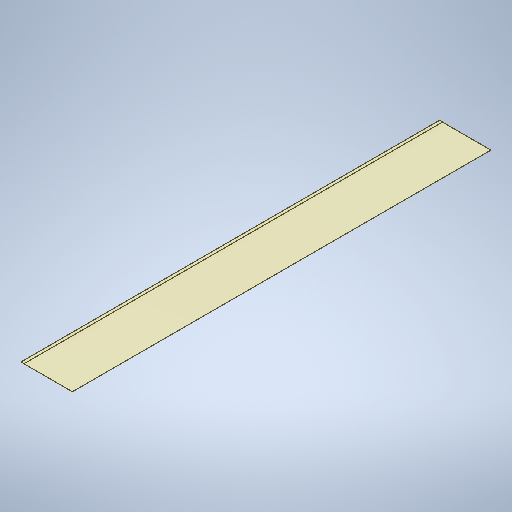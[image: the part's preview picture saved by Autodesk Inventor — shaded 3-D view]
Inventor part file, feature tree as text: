
AUTODESK INVENTOR PART (.ipt)
format: ipt  version: 2025 (Build 290162010, 162A)  size: 250,880 bytes
history: native  units: in
note: dims shown in document units (in); Inventor stores cm internally (conversion verified against a paired STEP export)
features: extrude x1, sketch x1
ambient origin geometry x8: Origin, YZ Plane, XZ Plane, XY Plane, X Axis, Y Axis, Z Axis, Center Point
bodies: Body1 (feature_tree)
feature tree (2):
  extrude  "Extrusion2"  Depth=0.125in
  sketch  "Sketch1"  dims[d0=2.0in d1=0.125in d2=0.125in d3=0.125in d4=0.125in d5=33.875in d8=292.512in d9=0.0in]
